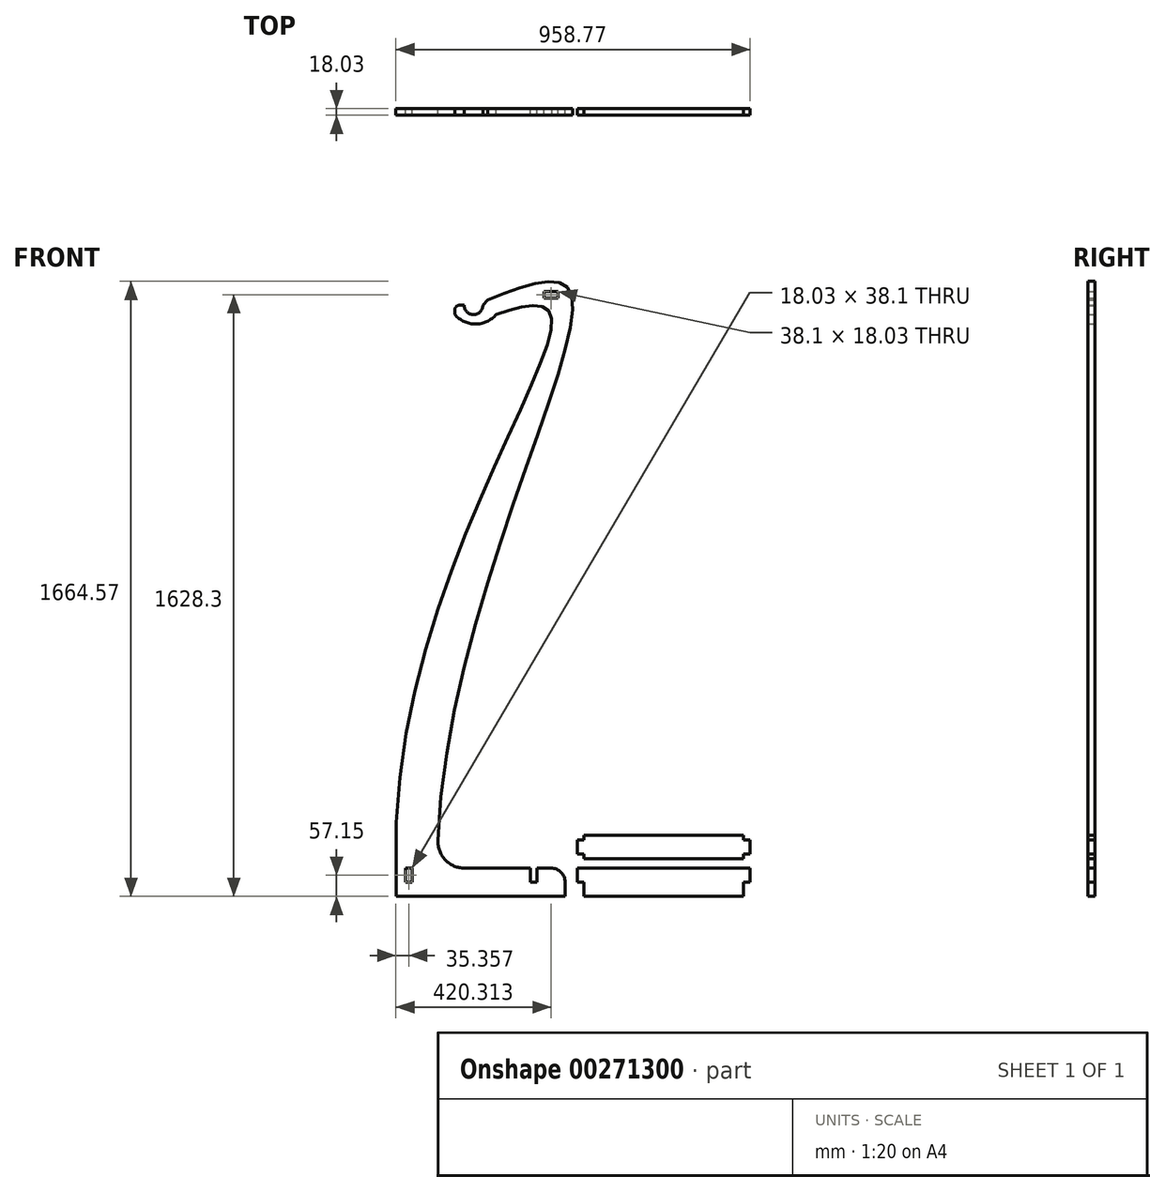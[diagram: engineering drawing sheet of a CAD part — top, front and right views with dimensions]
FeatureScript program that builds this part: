
annotation { "Feature Type Name" : "Feature", "Feature Type Description" : "" }
export const myFeature = defineFeature(function(context is Context, id is Id, definition is map)
    precondition{}
    {
        {
            var Q0;
            Q0=qCreatedBy(makeId("Front.planeOp"),FACE);
            var sketch = newSketch(context, id + "F0", { "sketchPlane" : qUnion([Q0])});
            skLineSegment(sketch, "E0.bottom", {"start": v(-209.55, 0) * mm, "end": v(209.55, 0) * mm});
            skLineSegment(sketch, "E0.top", {"start": v(-209.55, -76.2) * mm, "end": v(247.65, -76.2) * mm});
            skLineSegment(sketch, "E0.left", {"start": v(-209.55, 0) * mm, "end": v(-209.55, -76.2) * mm});
            skLineSegment(sketch, "E0.right", {"start": v(247.65, -38.1) * mm, "end": v(247.65, -76.2) * mm});
            skCircle(sketch, "E1", {"center": v(0, 1524) * mm, "radius": 25.4 * mm});
            skLineSegment(sketch, "E2", {"start": v(-25.4, 1524) * mm, "end": v(-38.1, 1524) * mm});
            skLineSegment(sketch, "E3", {"start": v(-50.8, 1511.3) * mm, "end": v(-50.8, 1498.6) * mm});
            skArc(sketch, "E4", {"start": v(-50.8, 1498.6) * mm, "mid": v(5.24, 1473.01) * mm, "end": v(61.29, 1498.6) * mm});
            skLineSegment(sketch, "E5", {"start": v(0, 1498.6) * mm, "end": v(0, 1473.2) * mm});
            skLineSegment(sketch, "E6", {"start": v(25.4, 1524) * mm, "end": v(38.1, 1538.2) * mm});
            skFitSpline(sketch, "E7", {"points": [v(38.1, 1538.2) * mm, v(259.29, 1565.86) * mm, v(-96.64, 75.13) * mm], "startDerivative": vector(1021.73, 409.71) * mm, "endDerivative": vector(-100.4, -2691.15) * mm});
            skFitSpline(sketch, "E8", {"points": [v(61.29, 1498.6) * mm, v(207.84, 1501.69) * mm, v(-209.55, 0) * mm], "startDerivative": vector(791.5, 308.4) * mm, "endDerivative": vector(99.16, -2859.47) * mm});
            skArc(sketch, "E9", {"start": v(-96.64, 75.13) * mm, "mid": v(-76.42, 22.18) * mm, "end": v(-24.26, 0) * mm});
            skPoint(sketch, "E10.visualSharp", {"position": v(247.65, 0) * mm});
            skArc(sketch, "E10.filletArc", {"start": v(247.65, -38.1) * mm, "mid": v(236.5, -11.16) * mm, "end": v(209.55, 0) * mm});
            skPoint(sketch, "E11.visualSharp", {"position": v(-50.8, 1524) * mm});
            skArc(sketch, "E11.filletArc", {"start": v(-38.1, 1524) * mm, "mid": v(-47.08, 1520.28) * mm, "end": v(-50.8, 1511.3) * mm});
            skLineSegment(sketch, "E12.bottom", {"start": v(-184.15, -38.1) * mm, "end": v(-166.12, -38.1) * mm});
            skLineSegment(sketch, "E12.top", {"start": v(-184.15, 0) * mm, "end": v(-166.12, 0) * mm});
            skLineSegment(sketch, "E12.left", {"start": v(-184.15, -38.1) * mm, "end": v(-184.15, 0) * mm});
            skLineSegment(sketch, "E12.right", {"start": v(-166.12, -38.1) * mm, "end": v(-166.12, 0) * mm});
            skLineSegment(sketch, "E13.bottom", {"start": v(153.42, 0) * mm, "end": v(171.45, 0) * mm});
            skLineSegment(sketch, "E13.top", {"start": v(153.42, -38.1) * mm, "end": v(171.45, -38.1) * mm});
            skLineSegment(sketch, "E13.left", {"start": v(153.42, 0) * mm, "end": v(153.42, -38.1) * mm});
            skLineSegment(sketch, "E13.right", {"start": v(171.45, 0) * mm, "end": v(171.45, -38.1) * mm});
            skLineSegment(sketch, "E14.bottom", {"start": v(298.45, 0) * mm, "end": v(730.25, 0) * mm});
            skLineSegment(sketch, "E14.top", {"start": v(298.45, -76.2) * mm, "end": v(730.25, -76.2) * mm});
            skLineSegment(sketch, "E14.left", {"start": v(298.45, 0) * mm, "end": v(298.45, -76.2) * mm});
            skLineSegment(sketch, "E14.right", {"start": v(730.25, 0) * mm, "end": v(730.25, -76.2) * mm});
            skLineSegment(sketch, "E15", {"start": v(298.45, -38.1) * mm, "end": v(280.42, -38.1) * mm});
            skLineSegment(sketch, "E16", {"start": v(280.42, -38.1) * mm, "end": v(280.42, 0) * mm});
            skLineSegment(sketch, "E17", {"start": v(280.42, 0) * mm, "end": v(298.45, 0) * mm});
            skLineSegment(sketch, "E18", {"start": v(730.25, 0) * mm, "end": v(748.28, 0) * mm});
            skLineSegment(sketch, "E19", {"start": v(748.28, 0) * mm, "end": v(748.28, -38.1) * mm});
            skLineSegment(sketch, "E20", {"start": v(748.28, -38.1) * mm, "end": v(730.25, -38.1) * mm});
            skLineSegment(sketch, "E21.bottom", {"start": v(190.77, 1561.12) * mm, "end": v(228.87, 1561.12) * mm});
            skLineSegment(sketch, "E21.top", {"start": v(190.77, 1543.08) * mm, "end": v(228.87, 1543.08) * mm});
            skLineSegment(sketch, "E21.left", {"start": v(190.77, 1561.12) * mm, "end": v(190.77, 1543.08) * mm});
            skLineSegment(sketch, "E21.right", {"start": v(228.87, 1561.12) * mm, "end": v(228.87, 1543.08) * mm});
            skLineSegment(sketch, "E22.bottom", {"start": v(298.45, 25.4) * mm, "end": v(730.25, 25.4) * mm});
            skLineSegment(sketch, "E22.top", {"start": v(298.45, 88.9) * mm, "end": v(730.25, 88.9) * mm});
            skLineSegment(sketch, "E22.left", {"start": v(298.45, 25.4) * mm, "end": v(298.45, 88.9) * mm});
            skLineSegment(sketch, "E22.right", {"start": v(730.25, 25.4) * mm, "end": v(730.25, 88.9) * mm});
            skLineSegment(sketch, "E23", {"start": v(298.45, 76.2) * mm, "end": v(280.42, 76.2) * mm});
            skLineSegment(sketch, "E24", {"start": v(280.42, 76.2) * mm, "end": v(280.42, 38.1) * mm});
            skLineSegment(sketch, "E25", {"start": v(280.42, 38.1) * mm, "end": v(298.45, 38.1) * mm});
            skPoint(sketch, "E26", {"position": v(280.42, 57.15) * mm});
            skPoint(sketch, "E27", {"position": v(298.45, 57.15) * mm});
            skLineSegment(sketch, "E28", {"start": v(514.35, 88.9) * mm, "end": v(514.35, 25.4) * mm, "construction": true});
            skLineSegment(sketch, "E29.MirrorCS", {"start": v(748.28, 76.2) * mm, "end": v(748.28, 38.1) * mm});
            skLineSegment(sketch, "E30.MirrorCS", {"start": v(748.28, 38.1) * mm, "end": v(730.25, 38.1) * mm});
            skPoint(sketch, "E31.MirrorP", {"position": v(730.25, 57.15) * mm});
            skLineSegment(sketch, "E32.MirrorCS", {"start": v(730.25, 76.2) * mm, "end": v(748.28, 76.2) * mm});
            skPoint(sketch, "E33.MirrorP", {"position": v(748.28, 57.15) * mm});
            skSolve(sketch);
        }
        {
            var Q0;
            {var subQ3=sQuery(id+"F0.wireOp",EDGE,"E14.bottom");Q0=makeQuery(id+"F0.imprint","IMPRINT",FACE,{"disambiguationData":[TD([[makeQuery(id+"F0.imprint","IMPRINT",EDGE,{"derivedFrom":subQ3}),-1.0]])]});}
            var Q1;
            {var subQ2=sQuery(id+"F0.wireOp",EDGE,"E15");Q1=makeQuery(id+"F0.imprint","IMPRINT",FACE,{"disambiguationData":[TD([[makeQuery(id+"F0.imprint","IMPRINT",EDGE,{"derivedFrom":subQ2}),-1.0]])]});}
            var Q2;
            {var subQ0=sQuery(id+"F0.wireOp",EDGE,"E18");Q2=makeQuery(id+"F0.imprint","IMPRINT",FACE,{"disambiguationData":[TD([[makeQuery(id+"F0.imprint","IMPRINT",EDGE,{"derivedFrom":subQ0}),-1.0]])]});}
            var Q3;
            Q3=makeQuery(id+"F0.imprint","IMPRINT",FACE,{"disambiguationData":[TD([[makeQuery(id+"F0.imprint","IMPRINT",EDGE,{"derivedFrom":sQuery(id+"F0.wireOp",EDGE,"E0.top")}),1.0]])]});
            var Q4;
            {var subQ2=sQuery(id+"F0.wireOp",EDGE,"E5");Q4=makeQuery(id+"F0.imprint","IMPRINT",FACE,{"disambiguationData":[TD([[makeQuery(id+"F0.imprint","IMPRINT",EDGE,{"derivedFrom":subQ2}),1.0]])]});}
            var Q5;
            {var subQ3=sQuery(id+"F0.wireOp",EDGE,"E2");Q5=makeQuery(id+"F0.imprint","IMPRINT",FACE,{"disambiguationData":[TD([[makeQuery(id+"F0.imprint","IMPRINT",EDGE,{"derivedFrom":subQ3}),1.0]])]});}
            var Q6;
            {var subQ0=sQuery(id+"F0.wireOp",EDGE,"E23");Q6=makeQuery(id+"F0.imprint","IMPRINT",FACE,{"disambiguationData":[TD([[makeQuery(id+"F0.imprint","IMPRINT",EDGE,{"derivedFrom":subQ0}),1.0]])]});}
            var Q7;
            {var subQ3=sQuery(id+"F0.wireOp",EDGE,"E22.bottom");Q7=makeQuery(id+"F0.imprint","IMPRINT",FACE,{"disambiguationData":[TD([[makeQuery(id+"F0.imprint","IMPRINT",EDGE,{"derivedFrom":subQ3}),1.0]])]});}
            var Q8;
            Q8=makeQuery(id+"F0.imprint","IMPRINT",FACE,{"disambiguationData":[TD([[makeQuery(id+"F0.imprint","IMPRINT",EDGE,{"derivedFrom":sQuery(id+"F0.wireOp",EDGE,"E29.MirrorCS")}),-1.0]])]});
            extrude(context, id + "F1", {"entities" : qUnion([Q0, Q1, Q2, Q3, Q4, Q5, Q6, Q7, Q8]), "depth" : 18.03 * mm});
        }
    });
